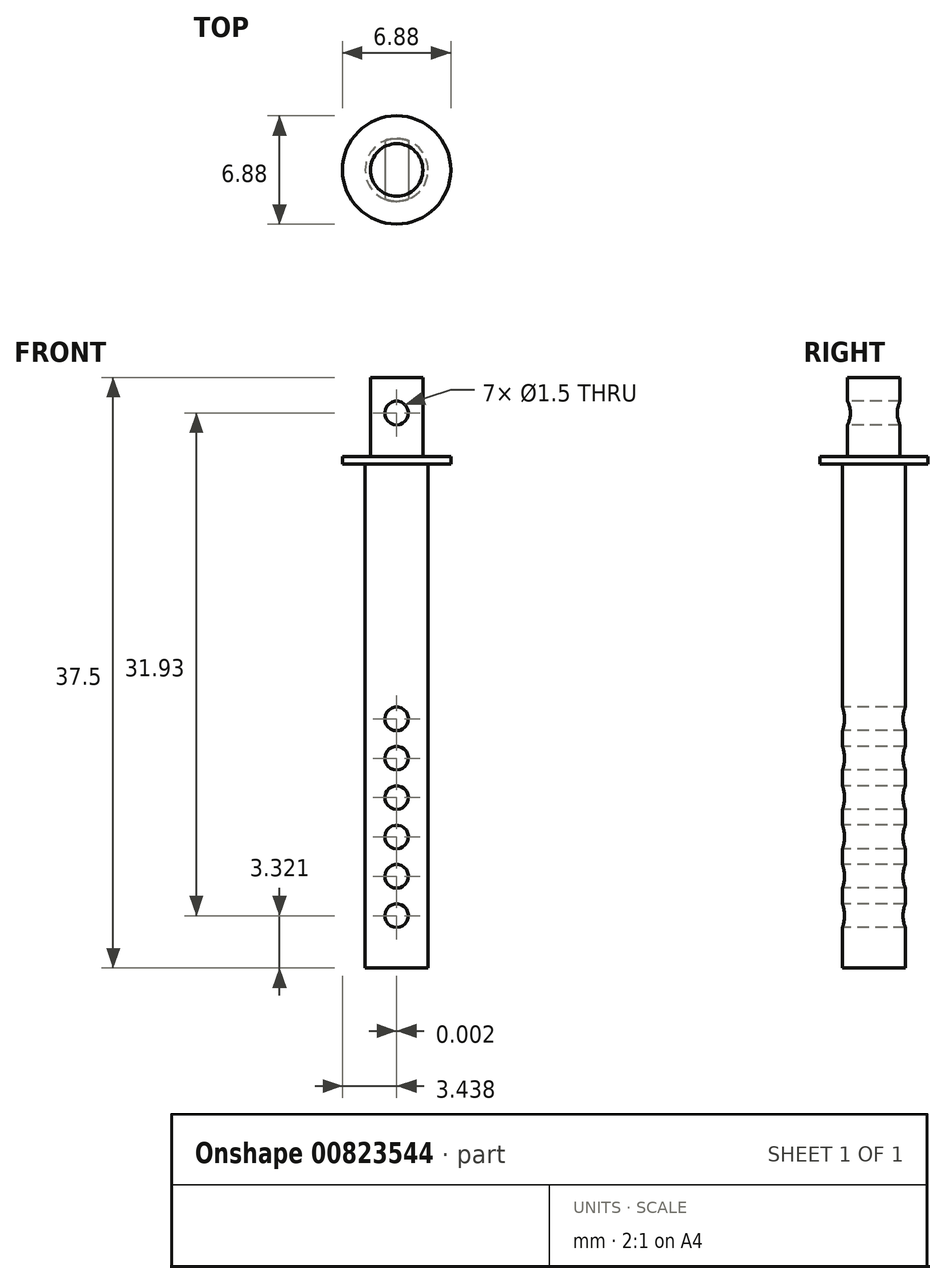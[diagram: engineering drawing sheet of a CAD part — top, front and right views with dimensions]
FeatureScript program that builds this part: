
annotation { "Feature Type Name" : "Feature", "Feature Type Description" : "" }
export const myFeature = defineFeature(function(context is Context, id is Id, definition is map)
    precondition{}
    {
        {
            var Q0;
            Q0=qCreatedBy(makeId("Top.planeOp"),FACE);
            var sketch = newSketch(context, id + "F0", { "sketchPlane" : qUnion([Q0])});
            skCircle(sketch, "E0", {"center": v(0, 0) * mm, "radius": 2 * mm});
            skSolve(sketch);
        }
        {
            var Q0;
            Q0=makeQuery(id+"F0.imprint","IMPRINT",FACE,{"disambiguationData":[TD([[makeQuery(id+"F0.imprint","IMPRINT",EDGE,{"derivedFrom":sQuery(id+"F0.wireOp",EDGE,"E0")}),1.0]])]});
            extrude(context, id + "F1", {"entities" : qUnion([Q0]), "depth" : 32 * mm, "offsetDistance" : 25 * mm});
        }
        {
            var Q0;
            Q0=makeQuery(id+"F1.opExtrude","CAP_FACE",FACE,{"disambiguationData":[OSD([sQuery(id+"F0.wireOp",EDGE,"E0")])],"isStart":false});
            var sketch = newSketch(context, id + "F2", { "sketchPlane" : qUnion([Q0])});
            skCircle(sketch, "E1", {"center": v(0, 0) * mm, "radius": 3.44 * mm});
            skSolve(sketch);
        }
        {
            var Q0;
            Q0=makeQuery(id+"F2.imprint","IMPRINT",FACE,{"disambiguationData":[TD([[makeQuery(id+"F2.imprint","IMPRINT",EDGE,{"derivedFrom":makeQuery(id+"F1.opExtrude","CAP_EDGE",EDGE,{"disambiguationData":[OSD([sQuery(id+"F0.wireOp",EDGE,"E0")])],"isStart":false})}),1.0]])]});
            var Q1;
            Q1=makeQuery(id+"F2.imprint","IMPRINT",FACE,{"disambiguationData":[TD([[makeQuery(id+"F2.imprint","IMPRINT",EDGE,{"derivedFrom":sQuery(id+"F2.wireOp",EDGE,"E1")}),1.0]])]});
            extrude(context, id + "F3", {"entities" : qUnion([Q0, Q1]), "operationType" : NewBodyOperationType.ADD, "depth" : .5 * mm, "offsetDistance" : 25 * mm});
        }
        {
            var Q0;
            Q0=makeQuery(id+"F3.opExtrude","CAP_FACE",FACE,{"disambiguationData":[OSD([sQuery(id+"F2.wireOp",EDGE,"E1")])],"isStart":false});
            var sketch = newSketch(context, id + "F4", { "sketchPlane" : qUnion([Q0])});
            skCircle(sketch, "E2", {"center": v(0, 0) * mm, "radius": 1.67 * mm});
            skSolve(sketch);
        }
        {
            var Q0;
            Q0=makeQuery(id+"F4.imprint","IMPRINT",FACE,{"disambiguationData":[TD([[makeQuery(id+"F4.imprint","IMPRINT",EDGE,{"derivedFrom":sQuery(id+"F4.wireOp",EDGE,"E2")}),1.0]])]});
            extrude(context, id + "F5", {"entities" : qUnion([Q0]), "operationType" : NewBodyOperationType.ADD, "depth" : 5 * mm, "offsetDistance" : 25 * mm});
        }
        {
            var Q0;
            Q0=qCreatedBy(makeId("Front.planeOp"),FACE);
            cPlane(context, id + "F6", {"entities" : qUnion([Q0]), "cplaneType" : CPlaneType.OFFSET, "offset" : 4 * mm, "width" : 150 * mm, "height" : 150 * mm});
        }
        {
            var Q0;
            Q0=qCreatedBy(id+"F6.planeOp",FACE);
            var sketch = newSketch(context, id + "F7", { "sketchPlane" : qUnion([Q0])});
            skCircle(sketch, "E3", {"center": v(0, 3.32) * mm, "radius": 0.75 * mm});
            skCircle(sketch, "E4", {"center": v(0, 5.82) * mm, "radius": 0.75 * mm});
            skCircle(sketch, "E5", {"center": v(0, 8.32) * mm, "radius": 0.75 * mm});
            skCircle(sketch, "E6", {"center": v(0, 10.82) * mm, "radius": 0.75 * mm});
            skCircle(sketch, "E7", {"center": v(0, 35.25) * mm, "radius": 0.75 * mm});
            skCircle(sketch, "E8", {"center": v(0, 13.32) * mm, "radius": 0.75 * mm});
            skCircle(sketch, "E9", {"center": v(0, 15.82) * mm, "radius": 0.75 * mm});
            skSolve(sketch);
        }
        {
            var Q0;
            Q0 = qSketchRegion(id + "F7", true);
            extrude(context, id + "F8", {"entities" : qUnion([Q0]), "operationType" : NewBodyOperationType.REMOVE, "oppositeDirection" : true, "depth" : 10 * mm, "offsetDistance" : 25 * mm});
        }
    });
